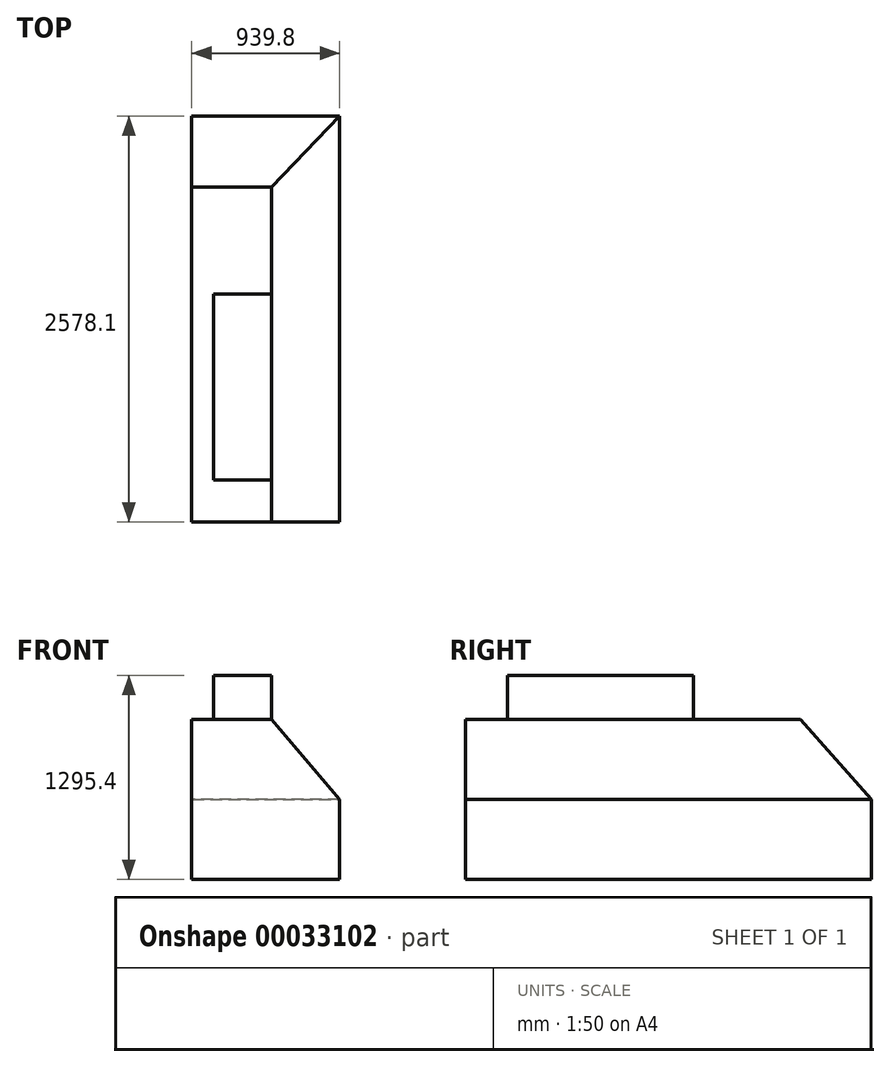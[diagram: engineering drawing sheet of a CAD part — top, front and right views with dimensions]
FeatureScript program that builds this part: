
annotation { "Feature Type Name" : "Feature", "Feature Type Description" : "" }
export const myFeature = defineFeature(function(context is Context, id is Id, definition is map)
    precondition{}
    {
        {
            var Q0;
            Q0=qCreatedBy(makeId("Front.planeOp"),FACE);
            var sketch = newSketch(context, id + "F0", { "sketchPlane" : qUnion([Q0])});
            skLineSegment(sketch, "E0.bottom", {"start": v(0, 0) * mm, "end": v(939.8, 0) * mm});
            skLineSegment(sketch, "E0.top", {"start": v(0, 1295.4) * mm, "end": v(939.8, 1295.4) * mm});
            skLineSegment(sketch, "E0.left", {"start": v(0, 0) * mm, "end": v(0, 1295.4) * mm});
            skLineSegment(sketch, "E0.right", {"start": v(939.8, 0) * mm, "end": v(939.8, 1295.4) * mm});
            skSolve(sketch);
        }
        {
            var Q0;
            Q0 = qSketchRegion(id + "F0", true);
            extrude(context, id + "F1", {"entities" : qUnion([Q0]), "depth" : 2578.1 * mm});
        }
        {
            var Q0;
            Q0=makeQuery(id+"F1.opExtrude","CAP_FACE",FACE,{"disambiguationData":[OSD([sQuery(id+"F0.wireOp",EDGE,"E0.bottom"),sQuery(id+"F0.wireOp",EDGE,"E0.top"),sQuery(id+"F0.wireOp",EDGE,"E0.left"),sQuery(id+"F0.wireOp",EDGE,"E0.right")])],"isStart":false});
            var sketch = newSketch(context, id + "F2", { "sketchPlane" : qUnion([Q0])});
            skLineSegment(sketch, "E1", {"start": v(0, 1295.4) * mm, "end": v(0, 1016) * mm});
            skLineSegment(sketch, "E2", {"start": v(0, 1016) * mm, "end": v(139.7, 1016) * mm});
            skLineSegment(sketch, "E3", {"start": v(139.7, 1016) * mm, "end": v(139.7, 1295.4) * mm});
            skLineSegment(sketch, "E4", {"start": v(139.7, 1295.4) * mm, "end": v(0, 1295.4) * mm});
            skSolve(sketch);
        }
        {
            var Q0;
            Q0 = qSketchRegion(id + "F2", true);
            extrude(context, id + "F3", {"entities" : qUnion([Q0]), "operationType" : NewBodyOperationType.REMOVE, "endBound" : BoundingType.UP_TO_NEXT, "oppositeDirection" : true, "depth" : 25.4 * mm});
        }
        {
            var Q0;
            Q0=makeQuery(id+"F1.opExtrude","CAP_FACE",FACE,{"disambiguationData":[OSD([sQuery(id+"F0.wireOp",EDGE,"E0.bottom"),sQuery(id+"F0.wireOp",EDGE,"E0.top"),sQuery(id+"F0.wireOp",EDGE,"E0.left"),sQuery(id+"F0.wireOp",EDGE,"E0.right")])],"isStart":false});
            var sketch = newSketch(context, id + "F4", { "sketchPlane" : qUnion([Q0])});
            skLineSegment(sketch, "E5", {"start": v(508, 1295.4) * mm, "end": v(508, 1016) * mm});
            skLineSegment(sketch, "E6", {"start": v(508, 1016) * mm, "end": v(939.8, 1016) * mm});
            skLineSegment(sketch, "E7", {"start": v(939.8, 1016) * mm, "end": v(939.8, 1295.4) * mm});
            skLineSegment(sketch, "E8", {"start": v(939.8, 1295.4) * mm, "end": v(508, 1295.4) * mm});
            skSolve(sketch);
        }
        {
            var Q0;
            Q0 = qSketchRegion(id + "F4", true);
            extrude(context, id + "F5", {"entities" : qUnion([Q0]), "operationType" : NewBodyOperationType.REMOVE, "endBound" : BoundingType.UP_TO_NEXT, "oppositeDirection" : true, "depth" : 25.4 * mm});
        }
        {
            var Q0;
            Q0=makeQuery(id+"F1.opExtrude","CAP_FACE",FACE,{"disambiguationData":[OSD([sQuery(id+"F0.wireOp",EDGE,"E0.bottom"),sQuery(id+"F0.wireOp",EDGE,"E0.top"),sQuery(id+"F0.wireOp",EDGE,"E0.left"),sQuery(id+"F0.wireOp",EDGE,"E0.right")])],"isStart":false});
            var sketch = newSketch(context, id + "F6", { "sketchPlane" : qUnion([Q0])});
            skLineSegment(sketch, "E9", {"start": v(508, 1016) * mm, "end": v(939.8, 1016) * mm});
            skLineSegment(sketch, "E10", {"start": v(939.8, 1016) * mm, "end": v(939.8, 508) * mm});
            skLineSegment(sketch, "E11", {"start": v(939.8, 508) * mm, "end": v(508, 1016) * mm});
            skSolve(sketch);
        }
        {
            var Q0;
            Q0 = qSketchRegion(id + "F6", true);
            extrude(context, id + "F7", {"entities" : qUnion([Q0]), "operationType" : NewBodyOperationType.REMOVE, "endBound" : BoundingType.UP_TO_NEXT, "oppositeDirection" : true, "depth" : 25.4 * mm});
        }
        {
            var Q0;
            Q0=qCreatedBy(makeId("Right.planeOp"),FACE);
            var sketch = newSketch(context, id + "F8", { "sketchPlane" : qUnion([Q0])});
            skLineSegment(sketch, "E12", {"start": v(0, 508) * mm, "end": v(0, 1016) * mm});
            skLineSegment(sketch, "E13", {"start": v(0, 1016) * mm, "end": v(-450.85, 1016) * mm});
            skLineSegment(sketch, "E14", {"start": v(-450.85, 1016) * mm, "end": v(0, 508) * mm});
            skSolve(sketch);
        }
        {
            var Q0;
            Q0 = qSketchRegion(id + "F8", true);
            extrude(context, id + "F9", {"entities" : qUnion([Q0]), "operationType" : NewBodyOperationType.REMOVE, "endBound" : BoundingType.UP_TO_NEXT, "depth" : 25.4 * mm});
        }
        {
            var Q0;
            Q0=makeQuery(id+"F5.boolean.opBoolean","COPY",FACE,{"derivedFrom":makeQuery(id+"F5.opExtrude","SWEPT_FACE",FACE,{"disambiguationData":[OSD([sQuery(id+"F4.wireOp",EDGE,"E5")])]})});
            var sketch = newSketch(context, id + "F10", { "sketchPlane" : qUnion([Q0])});
            skLineSegment(sketch, "E15", {"start": v(-1130.3, 1295.4) * mm, "end": v(0, 1295.4) * mm});
            skLineSegment(sketch, "E16", {"start": v(0, 1295.4) * mm, "end": v(0, 1016) * mm});
            skLineSegment(sketch, "E17", {"start": v(0, 1016) * mm, "end": v(-1130.3, 1016) * mm});
            skLineSegment(sketch, "E18", {"start": v(-1130.3, 1016) * mm, "end": v(-1130.3, 1295.4) * mm});
            skSolve(sketch);
        }
        {
            var Q0;
            Q0 = qSketchRegion(id + "F10", true);
            extrude(context, id + "F11", {"entities" : qUnion([Q0]), "operationType" : NewBodyOperationType.REMOVE, "endBound" : BoundingType.UP_TO_NEXT, "oppositeDirection" : true, "depth" : 25.4 * mm});
        }
        {
            var Q0;
            Q0=makeQuery(id+"F5.boolean.opBoolean","COPY",FACE,{"derivedFrom":makeQuery(id+"F5.opExtrude","SWEPT_FACE",FACE,{"disambiguationData":[OSD([sQuery(id+"F4.wireOp",EDGE,"E5")])]})});
            var sketch = newSketch(context, id + "F12", { "sketchPlane" : qUnion([Q0])});
            skLineSegment(sketch, "E19", {"start": v(-2578.1, 1295.4) * mm, "end": v(-2311.4, 1295.4) * mm});
            skLineSegment(sketch, "E20", {"start": v(-2311.4, 1295.4) * mm, "end": v(-2311.4, 1016) * mm});
            skLineSegment(sketch, "E21", {"start": v(-2311.4, 1016) * mm, "end": v(-2578.1, 1016) * mm});
            skLineSegment(sketch, "E22", {"start": v(-2578.1, 1016) * mm, "end": v(-2578.1, 1295.4) * mm});
            skSolve(sketch);
        }
        {
            var Q0;
            Q0 = qSketchRegion(id + "F12", true);
            extrude(context, id + "F13", {"entities" : qUnion([Q0]), "operationType" : NewBodyOperationType.REMOVE, "endBound" : BoundingType.UP_TO_NEXT, "oppositeDirection" : true, "depth" : 25.4 * mm});
        }
        {
            var Q0;
            Q0=makeQuery(id+"F1.opExtrude","SWEPT_FACE",FACE,{"disambiguationData":[OSD([sQuery(id+"F0.wireOp",EDGE,"E0.bottom")])]});
            var sketch = newSketch(context, id + "F14", { "sketchPlane" : qUnion([Q0])});
            skLineSegment(sketch, "E23.bottom", {"start": v(3.17, 2574.92) * mm, "end": v(936.62, 2574.92) * mm});
            skLineSegment(sketch, "E23.top", {"start": v(3.18, 3.18) * mm, "end": v(936.63, 3.18) * mm});
            skLineSegment(sketch, "E23.left", {"start": v(3.17, 2574.92) * mm, "end": v(3.17, 3.17) * mm});
            skLineSegment(sketch, "E23.right", {"start": v(936.62, 2574.92) * mm, "end": v(936.63, 3.17) * mm});
            skSolve(sketch);
        }
        {
            var Q0;
            Q0 = qSketchRegion(id + "F14", true);
            extrude(context, id + "F15", {"entities" : qUnion([Q0]), "operationType" : NewBodyOperationType.REMOVE, "oppositeDirection" : true, "depth" : 508 * mm});
        }
    });
